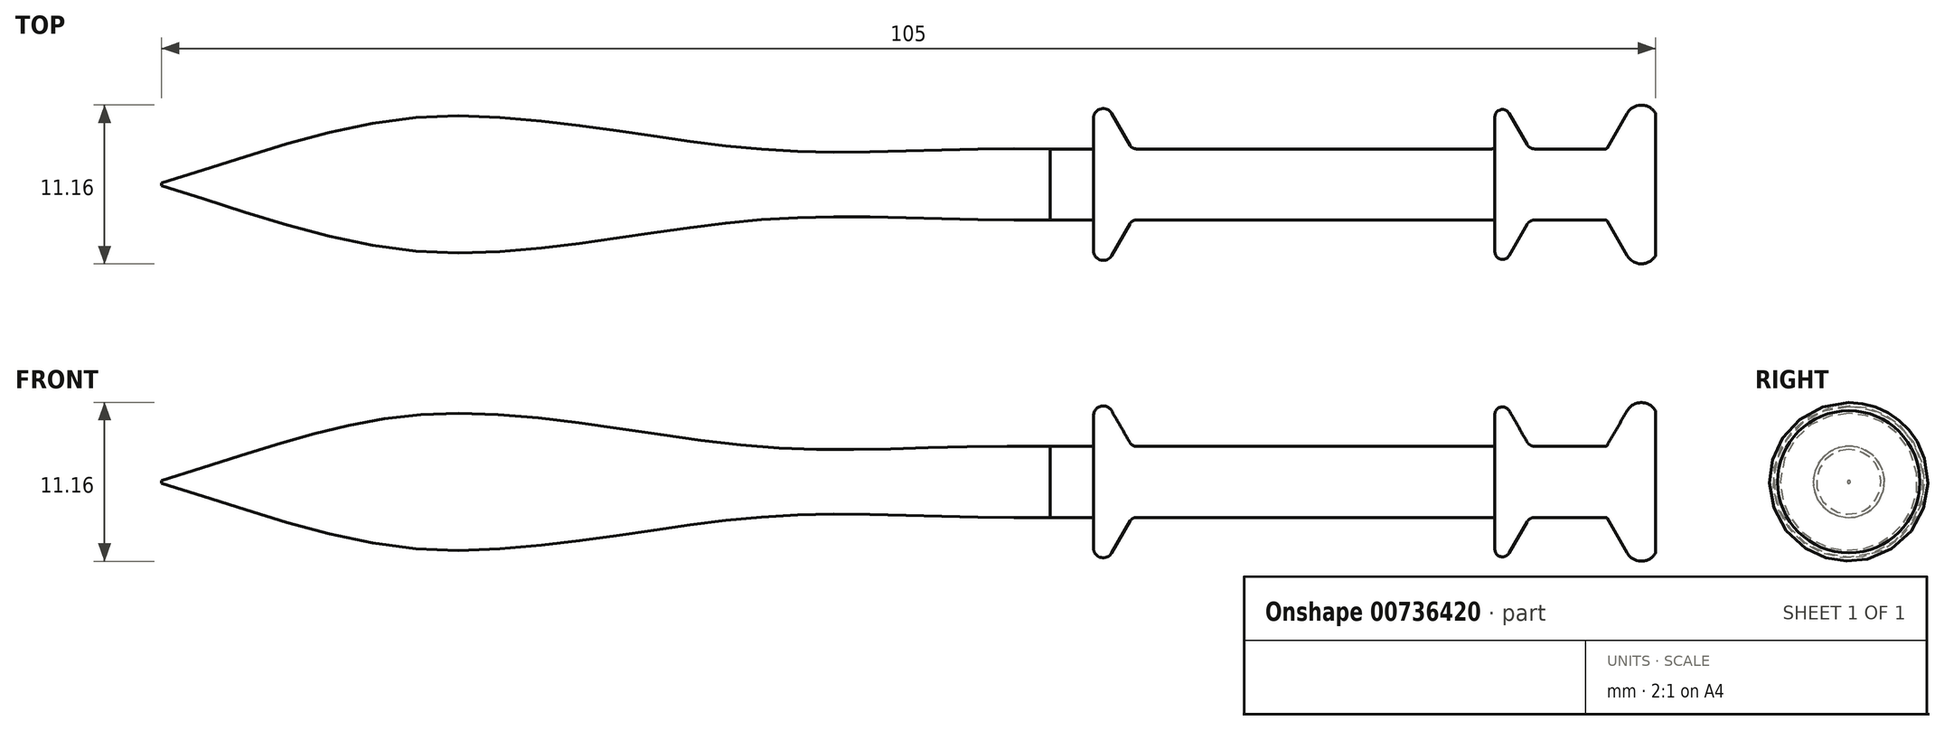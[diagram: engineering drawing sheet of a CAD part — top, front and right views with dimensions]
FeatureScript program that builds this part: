
annotation { "Feature Type Name" : "Feature", "Feature Type Description" : "" }
export const myFeature = defineFeature(function(context is Context, id is Id, definition is map)
    precondition{}
    {
        {
            var Q0;
            Q0=qCreatedBy(makeId("Front.planeOp"),FACE);
            var sketch = newSketch(context, id + "F0", { "sketchPlane" : qUnion([Q0])});
            skLineSegment(sketch, "E0", {"start": v(0, 0) * mm, "end": v(0, -5) * mm});
            skLineSegment(sketch, "E1", {"start": v(-2, -5) * mm, "end": v(-3.42, -2.55) * mm});
            skLineSegment(sketch, "E2", {"start": v(-3.5, -2.5) * mm, "end": v(-8.5, -2.5) * mm});
            skLineSegment(sketch, "E3", {"start": v(-9.02, -2.8) * mm, "end": v(-10.29, -5) * mm});
            skLineSegment(sketch, "E4", {"start": v(-11.3, -4.73) * mm, "end": v(-11.3, -2.7) * mm});
            skLineSegment(sketch, "E5", {"start": v(-11.5, -2.5) * mm, "end": v(-36.5, -2.5) * mm});
            skLineSegment(sketch, "E6", {"start": v(-36.93, -2.75) * mm, "end": v(-38.23, -5) * mm});
            skLineSegment(sketch, "E7", {"start": v(-39.5, -4.66) * mm, "end": v(-39.5, -2.5) * mm});
            skLineSegment(sketch, "E8", {"start": v(-105, -0.1) * mm, "end": v(-105, 0) * mm});
            skLineSegment(sketch, "E9", {"start": v(-105, 0) * mm, "end": v(0, 0) * mm});
            skArc(sketch, "E10", {"start": v(-2, -5) * mm, "mid": v(-1, -5.58) * mm, "end": v(0, -5) * mm});
            skArc(sketch, "E11", {"start": v(-11.3, -4.73) * mm, "mid": v(-10.9, -5.25) * mm, "end": v(-10.29, -5) * mm});
            skArc(sketch, "E12", {"start": v(-39.5, -4.66) * mm, "mid": v(-39, -5.32) * mm, "end": v(-38.23, -5) * mm});
            skPoint(sketch, "E13.visualSharp", {"position": v(-36.79, -2.5) * mm});
            skArc(sketch, "E13.filletArc", {"start": v(-36.5, -2.5) * mm, "mid": v(-36.75, -2.57) * mm, "end": v(-36.93, -2.75) * mm});
            skPoint(sketch, "E14.visualSharp", {"position": v(-11.3, -2.5) * mm});
            skArc(sketch, "E14.filletArc", {"start": v(-11.3, -2.7) * mm, "mid": v(-11.36, -2.56) * mm, "end": v(-11.5, -2.5) * mm});
            skPoint(sketch, "E15.visualSharp", {"position": v(-8.85, -2.5) * mm});
            skArc(sketch, "E15.filletArc", {"start": v(-8.5, -2.5) * mm, "mid": v(-8.8, -2.58) * mm, "end": v(-9.02, -2.8) * mm});
            skPoint(sketch, "E16.visualSharp", {"position": v(-3.44, -2.5) * mm});
            skArc(sketch, "E16.filletArc", {"start": v(-3.42, -2.55) * mm, "mid": v(-3.45, -2.51) * mm, "end": v(-3.5, -2.5) * mm});
            skLineSegment(sketch, "E17", {"start": v(-39.5, -2.5) * mm, "end": v(-42.55, -2.5) * mm});
            skFitSpline(sketch, "E18", {"points": [v(-42.55, -2.5) * mm, v(-63.2, -2.5) * mm, v(-85.46, -4.8) * mm, v(-105, -0.1) * mm], "startDerivative": vector(-71.04, -1.12) * mm, "endDerivative": vector(-66.74, 20.4) * mm});
            skSolve(sketch);
        }
        {
            var Q0;
            Q0 = qSketchRegion(id + "F0", true);
            var Q1;
            Q1=sQuery(id+"F0.wireOp",EDGE,"E9");
            revolve(context, id + "F1", {"surfaceOperationType" : NewSurfaceOperationType.NEW, "entities" : qUnion([Q0]), "axis" : qUnion([Q1]), "revolveType" : RevolveType.FULL});
        }
    });
